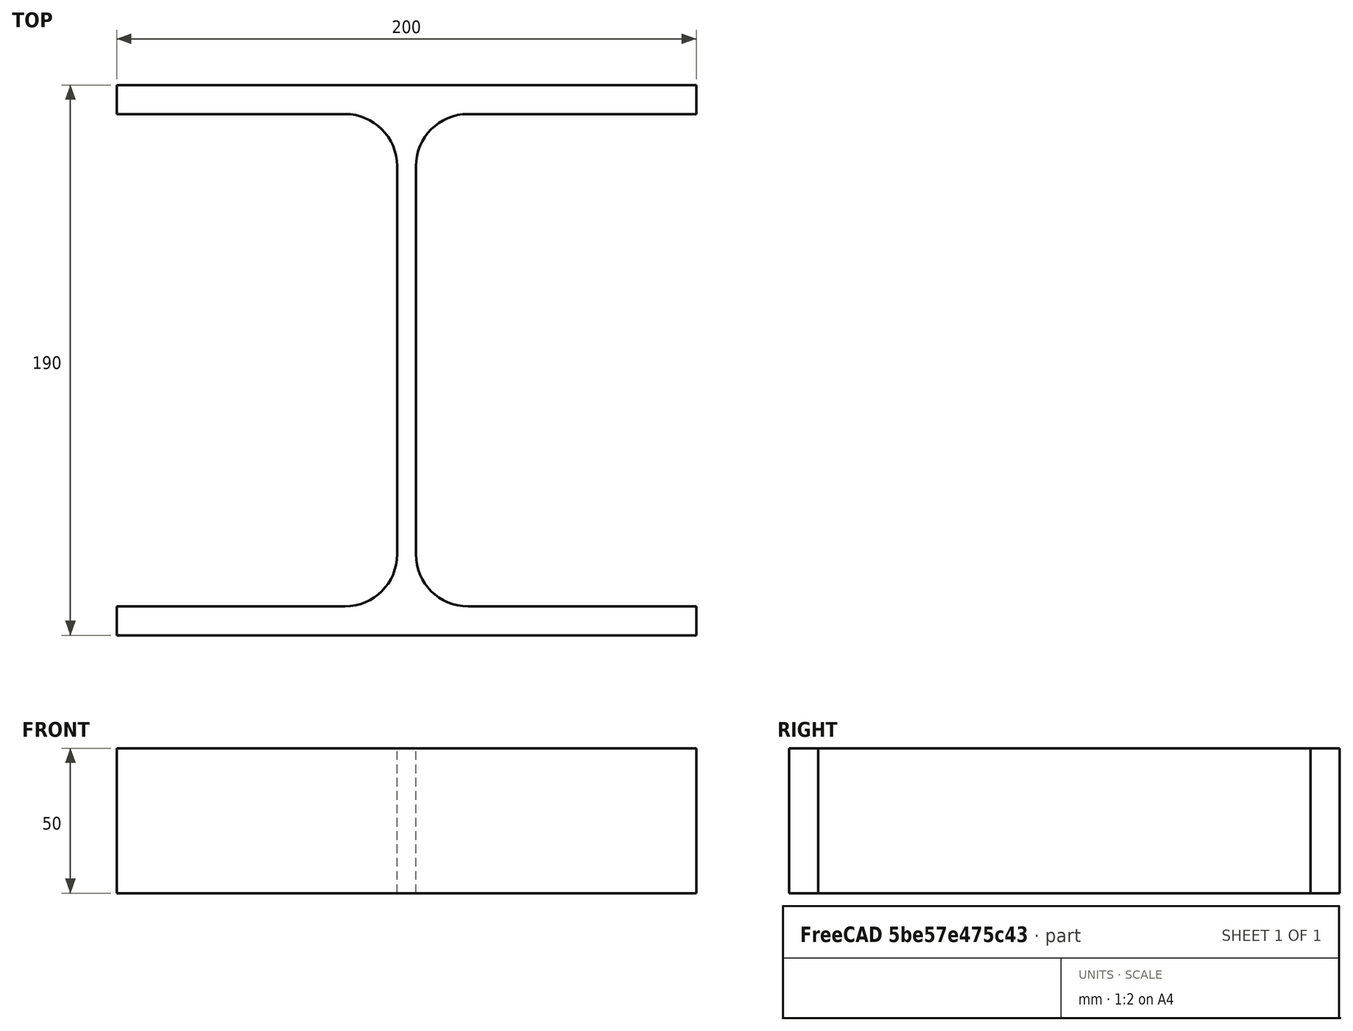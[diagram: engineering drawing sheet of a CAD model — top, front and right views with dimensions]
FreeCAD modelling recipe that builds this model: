
FCSTD DOCUMENT  (FreeCAD 0.15R4671 (Git))
Label: HE-A-Profile 200 DIN1025-3 S235JR
License: All rights reserved
LicenseURL: http://en.wikipedia.org/wiki/All_rights_reserved
objects: Sketcher::SketchObject×1, Part::Extrusion×1
note: 2 computed .brp shape members not serialized (recipe doc carries the construction recipe); baked Part::Feature solids carry a one-line shape summary decoded from their .brp

FEATURE [Sketcher::SketchObject] Sketch
  sketch-geometry (16):
    g0: LineSegment StartX=3.25 StartY=-67 StartZ=0 EndX=3.25 EndY=67 EndZ=0
    g1: LineSegment StartX=21.25 StartY=85 StartZ=0 EndX=100 EndY=85 EndZ=0
    g2: LineSegment StartX=100 StartY=85 StartZ=0 EndX=100 EndY=95 EndZ=0
    g3: LineSegment StartX=100 StartY=95 StartZ=0 EndX=-100 EndY=95 EndZ=0
    g4: LineSegment StartX=-100 StartY=95 StartZ=0 EndX=-100 EndY=85 EndZ=0
    g5: LineSegment StartX=-100 StartY=85 StartZ=0 EndX=-21.25 EndY=85 EndZ=0
    g6: LineSegment StartX=-3.25 StartY=67 StartZ=0 EndX=-3.25 EndY=-67 EndZ=0
    g7: LineSegment StartX=-21.25 StartY=-85 StartZ=0 EndX=-100 EndY=-85 EndZ=0
    g8: LineSegment StartX=-100 StartY=-85 StartZ=0 EndX=-100 EndY=-95 EndZ=0
    g9: LineSegment StartX=-100 StartY=-95 StartZ=0 EndX=100 EndY=-95 EndZ=0
    g10: LineSegment StartX=100 StartY=-95 StartZ=0 EndX=100 EndY=-85 EndZ=0
    g11: LineSegment StartX=100 StartY=-85 StartZ=0 EndX=21.25 EndY=-85 EndZ=0
    g12: ArcOfCircle CenterX=21.25 CenterY=67 CenterZ=0 NormalX=0 NormalY=0 NormalZ=1 Radius=18 StartAngle=1.5708 EndAngle=3.14159
    g13: ArcOfCircle CenterX=21.25 CenterY=-67 CenterZ=0 NormalX=0 NormalY=0 NormalZ=1 Radius=18 StartAngle=3.14159 EndAngle=4.71239
    g14: ArcOfCircle CenterX=-21.25 CenterY=67 CenterZ=0 NormalX=0 NormalY=0 NormalZ=1 Radius=18 StartAngle=0 EndAngle=1.5708
    g15: ArcOfCircle CenterX=-21.25 CenterY=-67 CenterZ=0 NormalX=0 NormalY=0 NormalZ=1 Radius=18 StartAngle=4.71239 EndAngle=6.28319
  constraints (42):
    c: Vertical(g0)
    c: Coincident(g2,g1)
    c: Vertical(g2)
    c: Coincident(g3,g2)
    c: Coincident(g4,g3)
    c: Vertical(g4)
    c: Coincident(g5,g4)
    c: Horizontal(g5)
    c: Vertical(g6)
    c: Horizontal(g7)
    c: Coincident(g8,g7)
    c: Vertical(g8)
    c: Coincident(g9,g8)
    c: Horizontal(g9)
    c: Coincident(g10,g9)
    c: Vertical(g10)
    c: Coincident(g11,g10)
    c: Horizontal(g11)
    c: Tangent(g1,g12) = 1.5708
    c: Tangent(g0,g12) = 1.5708
    c: Tangent(g0,g13) = 1.5708
    c: Tangent(g11,g13) = 1.5708
    c: Tangent(g5,g14) = 1.5708
    c: Tangent(g6,g14) = 1.5708
    c: Tangent(g6,g15) = 1.5708
    c: Tangent(g7,g15) = 1.5708
    c: Equal(g3,g9)
    c: Equal(g2,g4)
    c: Equal(g4,g8)
    c: Equal(g8,g10)
    c: Equal(g12,g14)
    c: Equal(g14,g15)
    c: Equal(g15,g13)
    c: Symmetric(g2,g3,g-2)
    c: Symmetric(g9,g8,g-2)
    c: Symmetric(g0,g6,g-2)
    c: Symmetric(g2,g9,g-1)
    c: DistanceY(g2,g9) = -190
    c: DistanceX(g3) = -200
    c: DistanceX(g0,g6) = -6.5
    c: DistanceY(g2) = 10
    c: Radius(g12) = 18
FEATURE [Part::Extrusion] Extrude  label="HE-A-Profile 200 DIN1025-3 S235JR"
  Base = -> Sketch
  Dir = (0,0,50)
  Solid = true
